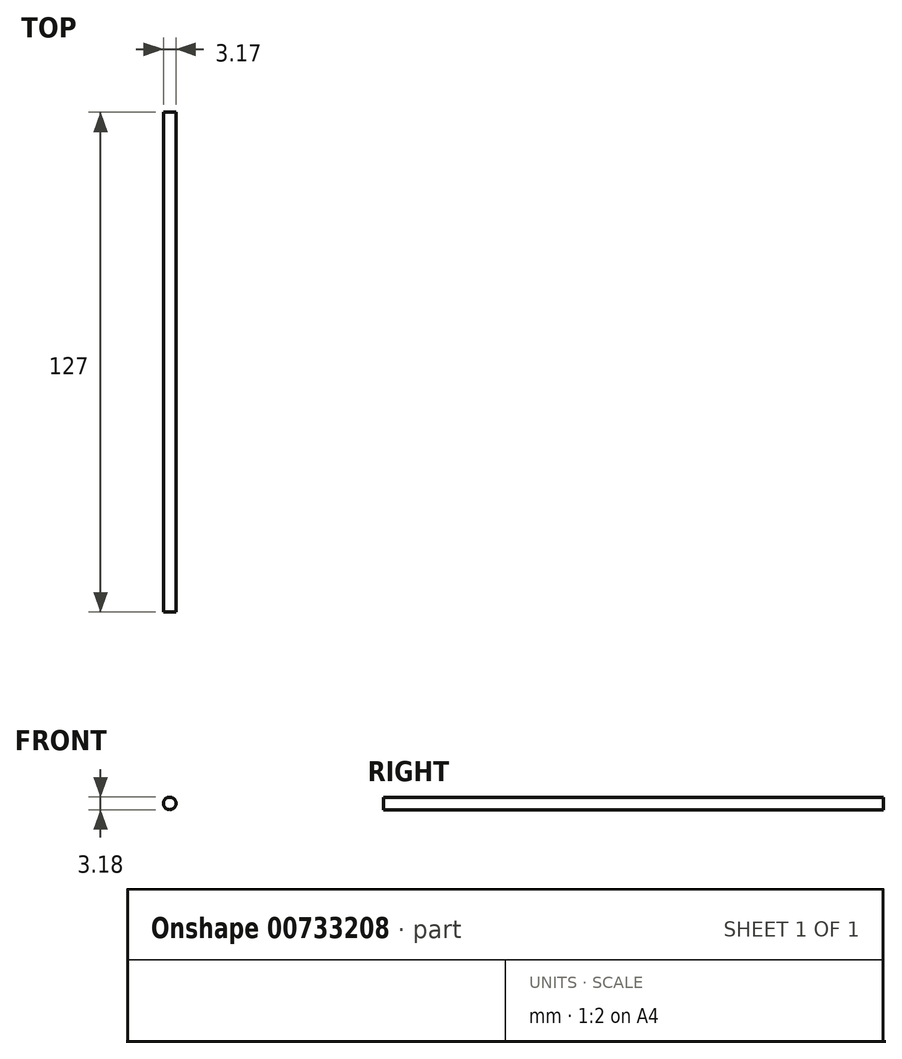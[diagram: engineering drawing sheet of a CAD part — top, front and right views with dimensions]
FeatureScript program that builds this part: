
annotation { "Feature Type Name" : "Feature", "Feature Type Description" : "" }
export const myFeature = defineFeature(function(context is Context, id is Id, definition is map)
    precondition{}
    {
        {
            var Q0;
            Q0=qCreatedBy(makeId("Front.planeOp"),FACE);
            var sketch = newSketch(context, id + "F0", { "sketchPlane" : qUnion([Q0])});
            skCircle(sketch, "E0", {"center": v(-33.24, 4.06) * mm, "radius": 1.59 * mm});
            skSolve(sketch);
        }
        {
            var Q0;
            Q0=makeQuery(id+"F0.imprint","IMPRINT",FACE,{"disambiguationData":[TD([[makeQuery(id+"F0.imprint","IMPRINT",EDGE,{"derivedFrom":sQuery(id+"F0.wireOp",EDGE,"E0")}),1.0]])]});
            extrude(context, id + "F1", {"entities" : qUnion([Q0]), "depth" : 127 * mm, "offsetDistance" : 25.4 * mm});
        }
    });
